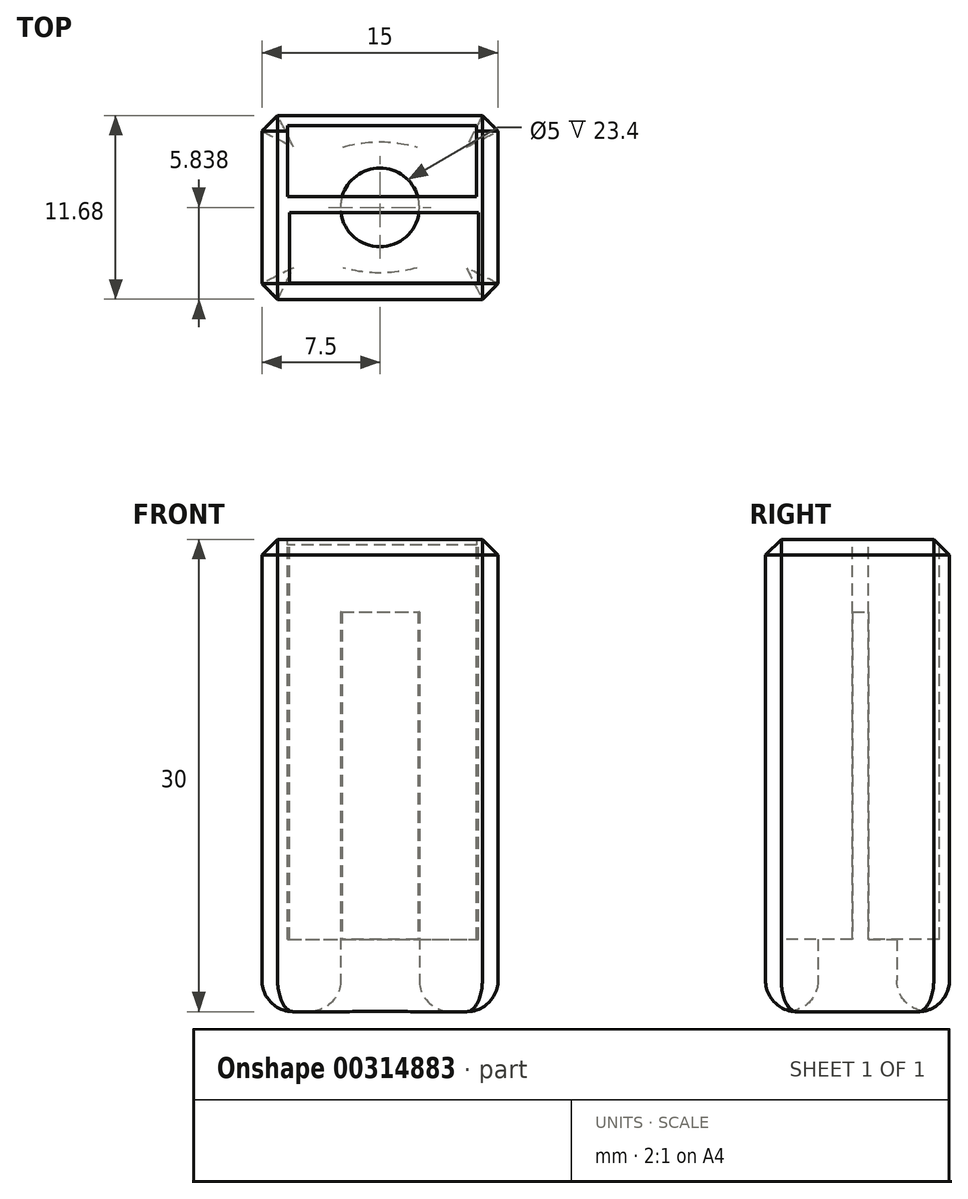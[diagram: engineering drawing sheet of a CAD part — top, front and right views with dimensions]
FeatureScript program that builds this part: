
annotation { "Feature Type Name" : "Feature", "Feature Type Description" : "" }
export const myFeature = defineFeature(function(context is Context, id is Id, definition is map)
    precondition{}
    {
        {
            var Q0;
            Q0=qCreatedBy(makeId("Front.planeOp"),FACE);
            var sketch = newSketch(context, id + "F0", { "sketchPlane" : qUnion([Q0])});
            skLineSegment(sketch, "E0.bottom", {"start": v(-7.5, -15) * mm, "end": v(7.5, -15) * mm});
            skLineSegment(sketch, "E0.top", {"start": v(-7.5, 15) * mm, "end": v(7.5, 15) * mm});
            skLineSegment(sketch, "E0.left", {"start": v(-7.5, -15) * mm, "end": v(-7.5, 15) * mm});
            skLineSegment(sketch, "E0.right", {"start": v(7.5, -15) * mm, "end": v(7.5, 15) * mm});
            skPoint(sketch, "E0.middle", {"position": v(0, 0) * mm});
            skSolve(sketch);
        }
        {
            var Q0;
            Q0 = qSketchRegion(id + "F0", true);
            extrude(context, id + "F1", {"entities" : qUnion([Q0]), "depth" : 11.68 * mm});
        }
        {
            var Q0;
            Q0=makeQuery(id+"F1.opExtrude","SWEPT_FACE",FACE,{"disambiguationData":[OSD([sQuery(id+"F0.wireOp",EDGE,"E0.top")])]});
            var sketch = newSketch(context, id + "F2", { "sketchPlane" : qUnion([Q0])});
            skLineSegment(sketch, "E1.bottom", {"start": v(-5.88, -0.64) * mm, "end": v(6.12, -0.64) * mm});
            skLineSegment(sketch, "E1.top", {"start": v(-5.88, -5.14) * mm, "end": v(6.12, -5.14) * mm});
            skLineSegment(sketch, "E1.left", {"start": v(-5.88, -0.64) * mm, "end": v(-5.88, -5.14) * mm});
            skLineSegment(sketch, "E1.right", {"start": v(6.12, -0.64) * mm, "end": v(6.12, -5.14) * mm});
            skLineSegment(sketch, "E2.bottom", {"start": v(-5.74, -6.16) * mm, "end": v(6.26, -6.16) * mm});
            skLineSegment(sketch, "E2.top", {"start": v(-5.74, -10.66) * mm, "end": v(6.26, -10.66) * mm});
            skLineSegment(sketch, "E2.left", {"start": v(-5.74, -6.16) * mm, "end": v(-5.74, -10.66) * mm});
            skLineSegment(sketch, "E2.right", {"start": v(6.26, -6.16) * mm, "end": v(6.26, -10.66) * mm});
            skSolve(sketch);
        }
        {
            var Q0;
            Q0=makeQuery(id+"F2.imprint","IMPRINT",FACE,{"disambiguationData":[TD([[makeQuery(id+"F2.imprint","IMPRINT",EDGE,{"derivedFrom":sQuery(id+"F2.wireOp",EDGE,"E1.bottom")}),-1.0]])]});
            var Q1;
            Q1=makeQuery(id+"F2.imprint","IMPRINT",FACE,{"disambiguationData":[TD([[makeQuery(id+"F2.imprint","IMPRINT",EDGE,{"derivedFrom":sQuery(id+"F2.wireOp",EDGE,"E2.bottom")}),-1.0]])]});
            extrude(context, id + "F3", {"entities" : qUnion([Q0, Q1]), "operationType" : NewBodyOperationType.REMOVE, "oppositeDirection" : true, "depth" : 25.4 * mm});
        }
        {
            var Q0;
            Q0=makeQuery(id+"F1.opExtrude","SWEPT_FACE",FACE,{"disambiguationData":[OSD([sQuery(id+"F0.wireOp",EDGE,"E0.bottom")])]});
            var sketch = newSketch(context, id + "F4", { "sketchPlane" : qUnion([Q0])});
            skLineSegment(sketch, "E3", {"start": v(-7.5, 11.68) * mm, "end": v(7.5, 0) * mm, "construction": true});
            skLineSegment(sketch, "E4", {"start": v(7.5, 11.68) * mm, "end": v(-7.5, 0) * mm, "construction": true});
            skCircle(sketch, "E5", {"center": v(0, 5.84) * mm, "radius": 2.5 * mm});
            skSolve(sketch);
        }
        {
            var Q0;
            Q0=makeQuery(id+"F4.imprint","IMPRINT",FACE,{"disambiguationData":[TD([[makeQuery(id+"F4.imprint","IMPRINT",EDGE,{"derivedFrom":sQuery(id+"F4.wireOp",EDGE,"E5")}),1.0]])]});
            var Q1;
            Q1=sQuery(id+"F4.wireOp",EDGE,"E5");
            extrude(context, id + "F5", {"entities" : qUnion([Q0]), "operationType" : NewBodyOperationType.REMOVE, "surfaceEntities" : qUnion([Q1]), "oppositeDirection" : true, "depth" : 25.4 * mm});
        }
        {
            var Q0;
            Q0=makeQuery(id+"F1.opExtrude","SWEPT_FACE",FACE,{"disambiguationData":[OSD([sQuery(id+"F0.wireOp",EDGE,"E0.bottom")])]});
            fillet(context, id + "F6", {"entities" : qUnion([Q0]), "radius" : 2 * mm, "tangentPropagation" : true, "allowEdgeOverflow" : false});
        }
        {
            var Q0;
            Q0=makeQuery(id+"F1.opExtrude","CAP_EDGE",EDGE,{"disambiguationData":[OSD([sQuery(id+"F0.wireOp",EDGE,"E0.top")])],"isStart":false});
            var Q1;
            Q1=makeQuery(id+"F1.opExtrude","SWEPT_EDGE",EDGE,{"disambiguationData":[OSD([sQuery(id+"F0.wireOp",EDGE,"E0.top"),sQuery(id+"F0.wireOp",EDGE,"E0.right")])]});
            var Q2;
            Q2=makeQuery(id+"F1.opExtrude","CAP_EDGE",EDGE,{"disambiguationData":[OSD([sQuery(id+"F0.wireOp",EDGE,"E0.top")])],"isStart":true});
            var Q3;
            Q3=makeQuery(id+"F1.opExtrude","SWEPT_EDGE",EDGE,{"disambiguationData":[OSD([sQuery(id+"F0.wireOp",EDGE,"E0.top"),sQuery(id+"F0.wireOp",EDGE,"E0.left")])]});
            var Q4;
            Q4=makeQuery(id+"F1.opExtrude","CAP_EDGE",EDGE,{"disambiguationData":[OSD([sQuery(id+"F0.wireOp",EDGE,"E0.left")])],"isStart":false});
            var Q5;
            Q5=makeQuery(id+"F1.opExtrude","CAP_EDGE",EDGE,{"disambiguationData":[OSD([sQuery(id+"F0.wireOp",EDGE,"E0.left")])],"isStart":true});
            var Q6;
            Q6=makeQuery(id+"F1.opExtrude","CAP_EDGE",EDGE,{"disambiguationData":[OSD([sQuery(id+"F0.wireOp",EDGE,"E0.right")])],"isStart":false});
            var Q7;
            Q7=makeQuery(id+"F1.opExtrude","CAP_EDGE",EDGE,{"disambiguationData":[OSD([sQuery(id+"F0.wireOp",EDGE,"E0.right")])],"isStart":true});
            chamfer(context, id + "F7", {"entities" : qUnion([Q0, Q1, Q2, Q3, Q4, Q5, Q6, Q7]), "width" : 1 * mm, "tangentPropagation" : true});
        }
    });
